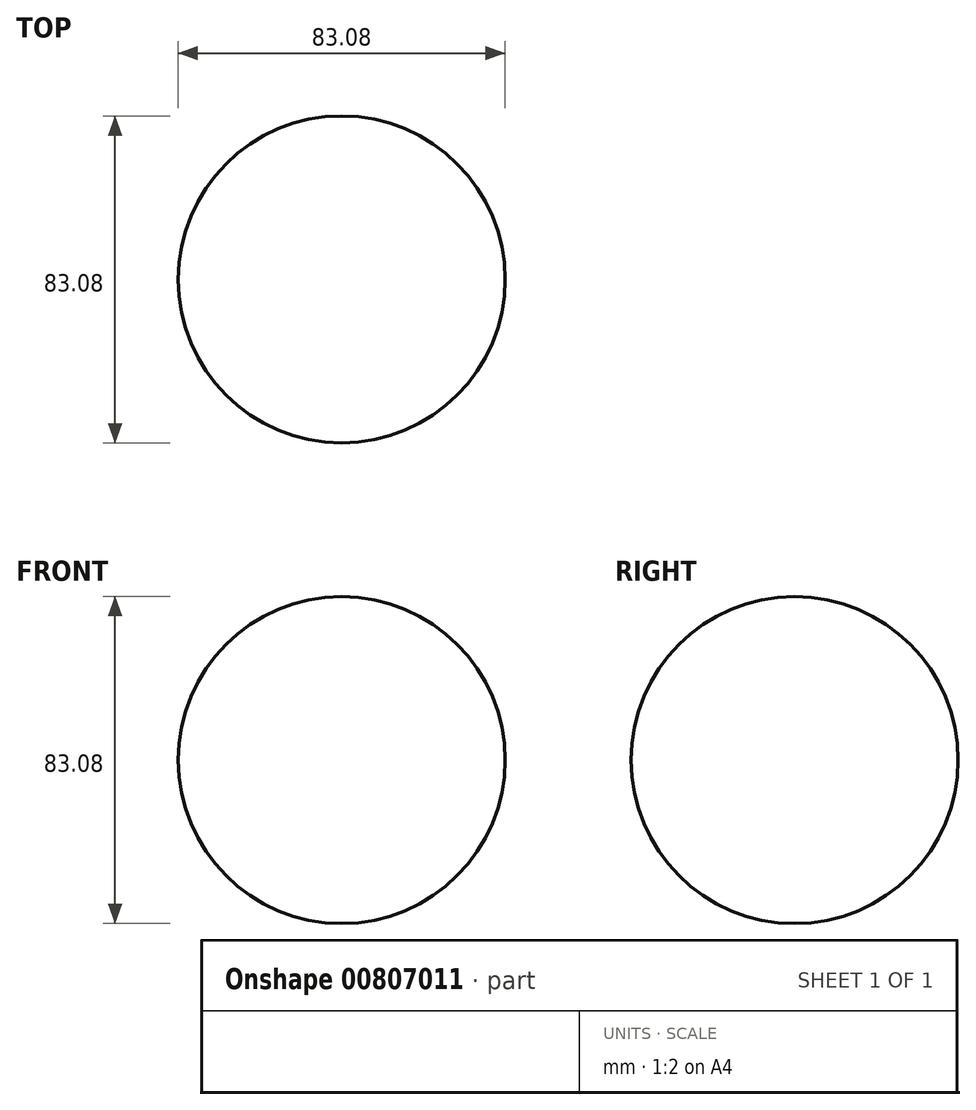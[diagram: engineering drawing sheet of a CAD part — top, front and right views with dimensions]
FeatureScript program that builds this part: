
annotation { "Feature Type Name" : "Feature", "Feature Type Description" : "" }
export const myFeature = defineFeature(function(context is Context, id is Id, definition is map)
    precondition{}
    {
        {
            var Q0;
            Q0=qCreatedBy(makeId("Front.planeOp"),FACE);
            var sketch = newSketch(context, id + "F0", { "sketchPlane" : qUnion([Q0])});
            skCircle(sketch, "E0", {"center": v(0, 0) * mm, "radius": 41.54 * mm});
            skLineSegment(sketch, "E1", {"start": v(0, 51.24) * mm, "end": v(0, -59.72) * mm});
            skSolve(sketch);
        }
        {
            var Q0;
            {var subQ0=sQuery(id+"F0.wireOp",EDGE,"E1");var subQ1=sQuery(id+"F0.wireOp",EDGE,"E0");var subQ2=makeQuery(id+"F0.imprint","INTERSECT",VERTEX,{"disambiguationData":[OD(0.0)],"derivedFrom":[subQ1,subQ0]});Q0=makeQuery(id+"F0.imprint","IMPRINT",FACE,{"disambiguationData":[TD([[makeQuery(id+"F0.imprint","IMPRINT",EDGE,{"disambiguationData":[TD([[subQ2,-1.0]])],"derivedFrom":subQ1}),1.0]])]});}
            var Q1;
            Q1=sQuery(id+"F0.wireOp",EDGE,"E1");
            revolve(context, id + "F1", {"surfaceOperationType" : NewSurfaceOperationType.NEW, "entities" : qUnion([Q0]), "axis" : qUnion([Q1]), "revolveType" : RevolveType.FULL});
        }
    });
